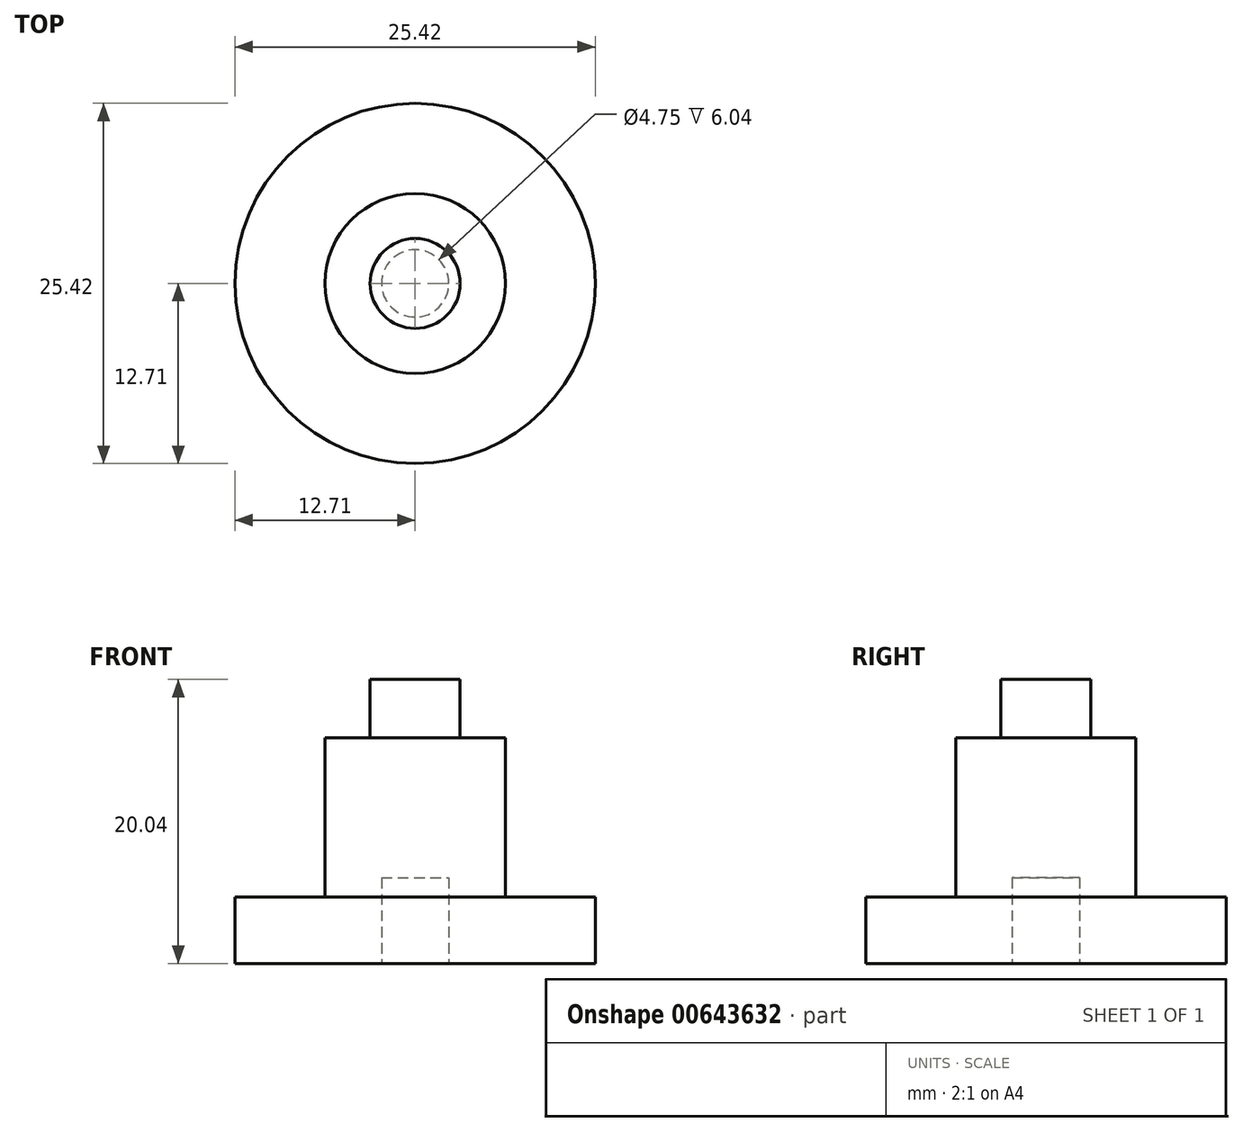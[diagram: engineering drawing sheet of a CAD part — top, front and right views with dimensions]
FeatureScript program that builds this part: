
annotation { "Feature Type Name" : "Feature", "Feature Type Description" : "" }
export const myFeature = defineFeature(function(context is Context, id is Id, definition is map)
    precondition{}
    {
        {
            var Q0;
            Q0=qCreatedBy(makeId("Top.planeOp"),FACE);
            var sketch = newSketch(context, id + "F0", { "sketchPlane" : qUnion([Q0])});
            skCircle(sketch, "E0", {"center": v(0, 0) * mm, "radius": 12.7 * mm});
            skSolve(sketch);
        }
        {
            var Q0;
            Q0=makeQuery(id+"F0.imprint","IMPRINT",FACE,{"disambiguationData":[TD([[makeQuery(id+"F0.imprint","IMPRINT",EDGE,{"derivedFrom":sQuery(id+"F0.wireOp",EDGE,"E0")}),1.0]])]});
            extrude(context, id + "F1", {"entities" : qUnion([Q0]), "depth" : 4.7 * mm, "offsetDistance" : 25 * mm});
        }
        {
            var Q0;
            Q0=makeQuery(id+"F1.opExtrude","CAP_FACE",FACE,{"disambiguationData":[OSD([sQuery(id+"F0.wireOp",EDGE,"E0")])],"isStart":false});
            var sketch = newSketch(context, id + "F2", { "sketchPlane" : qUnion([Q0])});
            skCircle(sketch, "E1", {"center": v(0, 0) * mm, "radius": 6.35 * mm});
            skSolve(sketch);
        }
        {
            var Q0;
            Q0=makeQuery(id+"F2.imprint","IMPRINT",FACE,{"disambiguationData":[TD([[makeQuery(id+"F2.imprint","IMPRINT",EDGE,{"derivedFrom":sQuery(id+"F2.wireOp",EDGE,"E1")}),1.0]])]});
            extrude(context, id + "F3", {"entities" : qUnion([Q0]), "operationType" : NewBodyOperationType.ADD, "depth" : 11.22 * mm, "offsetDistance" : 25 * mm});
        }
        {
            var Q0;
            Q0=makeQuery(id+"F3.opExtrude","CAP_FACE",FACE,{"disambiguationData":[OSD([sQuery(id+"F2.wireOp",EDGE,"E1")])],"isStart":false});
            var sketch = newSketch(context, id + "F4", { "sketchPlane" : qUnion([Q0])});
            skCircle(sketch, "E2", {"center": v(0, 0) * mm, "radius": 3.18 * mm});
            skSolve(sketch);
        }
        {
            var Q0;
            Q0=makeQuery(id+"F4.imprint","IMPRINT",FACE,{"disambiguationData":[TD([[makeQuery(id+"F4.imprint","IMPRINT",EDGE,{"derivedFrom":sQuery(id+"F4.wireOp",EDGE,"E2")}),1.0]])]});
            extrude(context, id + "F5", {"entities" : qUnion([Q0]), "operationType" : NewBodyOperationType.ADD, "depth" : 4.12 * mm, "offsetDistance" : 25 * mm});
        }
        {
            var Q0;
            Q0=makeQuery(id+"F1.opExtrude","CAP_FACE",FACE,{"disambiguationData":[OSD([sQuery(id+"F0.wireOp",EDGE,"E0")])],"isStart":true});
            var sketch = newSketch(context, id + "F6", { "sketchPlane" : qUnion([Q0])});
            skCircle(sketch, "E3", {"center": v(0, 0) * mm, "radius": 2.38 * mm});
            skSolve(sketch);
        }
        {
            var Q0;
            Q0=makeQuery(id+"F6.imprint","IMPRINT",FACE,{"disambiguationData":[TD([[makeQuery(id+"F6.imprint","IMPRINT",EDGE,{"derivedFrom":sQuery(id+"F6.wireOp",EDGE,"E3")}),1.0]])]});
            var Q1;
            Q1=sQuery(id+"F6.wireOp",EDGE,"E3");
            extrude(context, id + "F7", {"entities" : qUnion([Q0]), "operationType" : NewBodyOperationType.REMOVE, "surfaceEntities" : qUnion([Q1]), "oppositeDirection" : true, "depth" : 6.04 * mm, "offsetDistance" : 25 * mm});
        }
    });
